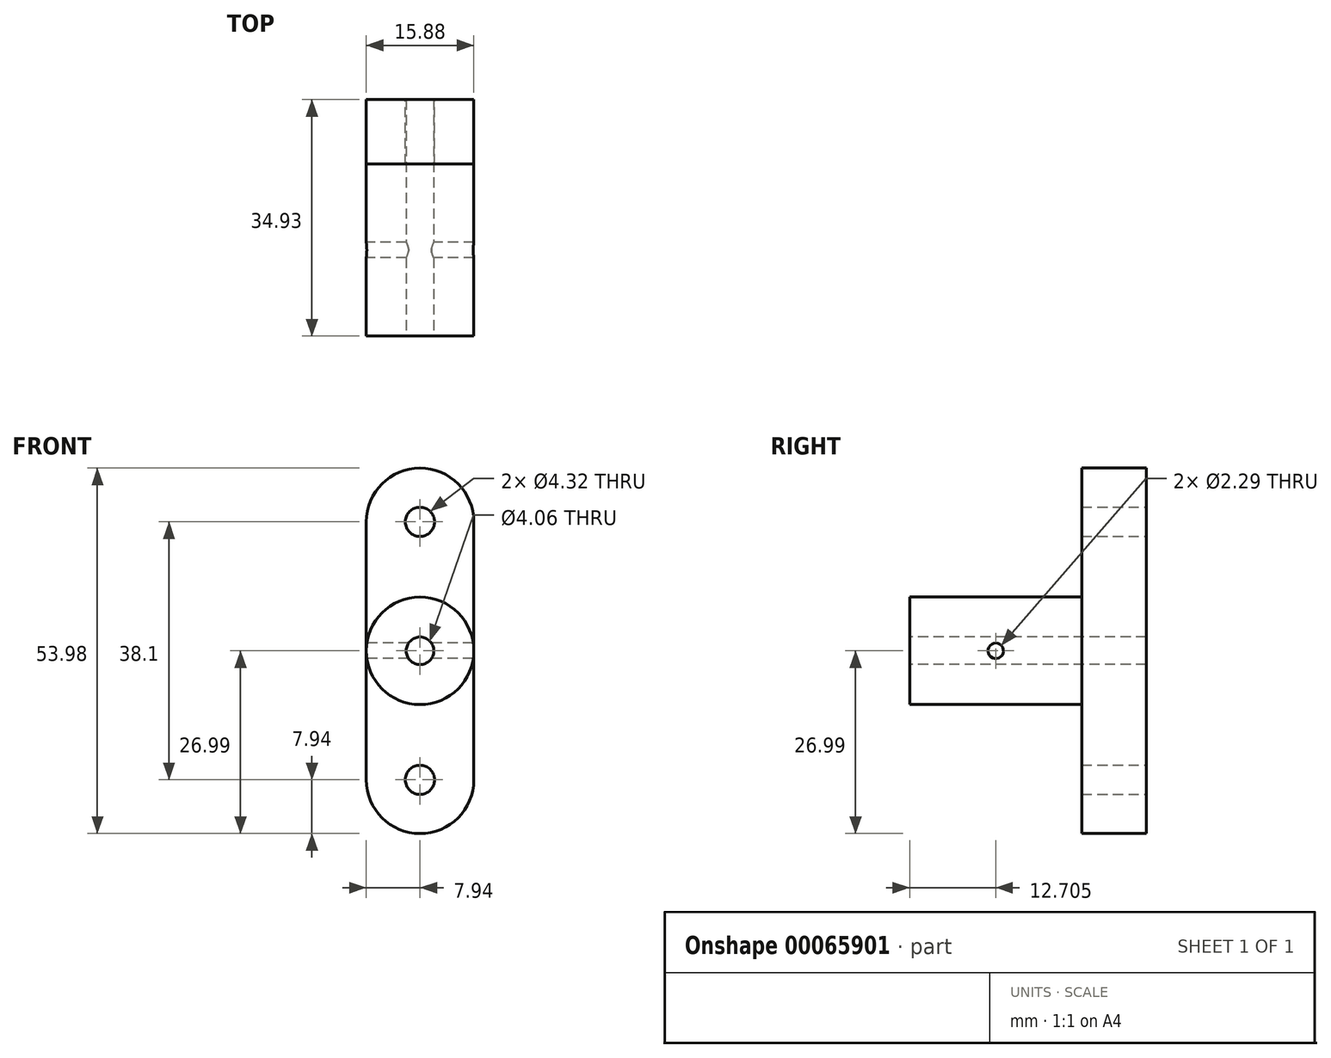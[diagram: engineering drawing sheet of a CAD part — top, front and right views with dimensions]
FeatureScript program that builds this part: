
annotation { "Feature Type Name" : "Feature", "Feature Type Description" : "" }
export const myFeature = defineFeature(function(context is Context, id is Id, definition is map)
    precondition{}
    {
        {
            var Q0;
            Q0=qCreatedBy(makeId("Front.planeOp"),FACE);
            var sketch = newSketch(context, id + "F0", { "sketchPlane" : qUnion([Q0])});
            skLineSegment(sketch, "E0.rect.bottom", {"start": v(7.94, 19.05) * mm, "end": v(-7.94, 19.05) * mm});
            skLineSegment(sketch, "E0.rect.top", {"start": v(7.94, -19.05) * mm, "end": v(-7.94, -19.05) * mm});
            skLineSegment(sketch, "E0.rect.left", {"start": v(7.94, 19.05) * mm, "end": v(7.94, -19.05) * mm});
            skLineSegment(sketch, "E0.rect.right", {"start": v(-7.94, 19.05) * mm, "end": v(-7.94, -19.05) * mm});
            skPoint(sketch, "E0.rect.middle", {"position": v(0, 0) * mm});
            skArc(sketch, "E1", {"start": v(-7.94, 19.05) * mm, "mid": v(0, 26.99) * mm, "end": v(7.94, 19.05) * mm});
            skArc(sketch, "E2", {"start": v(-7.94, -19.05) * mm, "mid": v(0, -26.99) * mm, "end": v(7.94, -19.05) * mm});
            skCircle(sketch, "E3", {"center": v(0, 19.05) * mm, "radius": 2.16 * mm});
            skCircle(sketch, "E4", {"center": v(0, -19.05) * mm, "radius": 2.16 * mm});
            skSolve(sketch);
        }
        {
            var Q0;
            Q0 = qSketchRegion(id + "F0", true);
            extrude(context, id + "F1", {"entities" : qUnion([Q0]), "depth" : 9.52 * mm});
        }
        {
            var Q0;
            Q0=makeQuery(id+"F1.opExtrude","CAP_FACE",FACE,{"disambiguationData":[OSD([sQuery(id+"F0.wireOp",EDGE,"E0.rect.left"),sQuery(id+"F0.wireOp",EDGE,"E0.rect.right"),sQuery(id+"F0.wireOp",EDGE,"E1"),sQuery(id+"F0.wireOp",EDGE,"E2"),sQuery(id+"F0.wireOp",EDGE,"E3"),sQuery(id+"F0.wireOp",EDGE,"E4")])],"isStart":false});
            var sketch = newSketch(context, id + "F2", { "sketchPlane" : qUnion([Q0])});
            skCircle(sketch, "E5", {"center": v(0, 0) * mm, "radius": 7.94 * mm});
            skSolve(sketch);
        }
        {
            var Q0;
            Q0 = qSketchRegion(id + "F2", true);
            extrude(context, id + "F3", {"entities" : qUnion([Q0]), "operationType" : NewBodyOperationType.ADD, "depth" : 25.4 * mm});
        }
        {
            var Q0;
            Q0=makeQuery(id+"F3.opExtrude","CAP_FACE",FACE,{"disambiguationData":[OSD([sQuery(id+"F2.wireOp",EDGE,"E5")])],"isStart":false});
            var sketch = newSketch(context, id + "F4", { "sketchPlane" : qUnion([Q0])});
            skCircle(sketch, "E6", {"center": v(0, 0) * mm, "radius": 2.03 * mm});
            skSolve(sketch);
        }
        {
            var Q0;
            Q0 = qSketchRegion(id + "F4", true);
            extrude(context, id + "F5", {"entities" : qUnion([Q0]), "operationType" : NewBodyOperationType.REMOVE, "endBound" : BoundingType.THROUGH_ALL, "oppositeDirection" : true, "depth" : 25.4 * mm});
        }
        {
            var Q0;
            Q0=makeQuery(id+"F1.opExtrude","SWEPT_FACE",FACE,{"disambiguationData":[OSD([sQuery(id+"F0.wireOp",EDGE,"E0.rect.right")])]});
            var sketch = newSketch(context, id + "F6", { "sketchPlane" : qUnion([Q0])});
            skCircle(sketch, "E7", {"center": v(22.23, 0) * mm, "radius": 1.14 * mm});
            skSolve(sketch);
        }
        {
            var Q0;
            Q0 = qSketchRegion(id + "F6", true);
            extrude(context, id + "F7", {"entities" : qUnion([Q0]), "operationType" : NewBodyOperationType.REMOVE, "oppositeDirection" : true, "depth" : 25.4 * mm});
        }
    });
